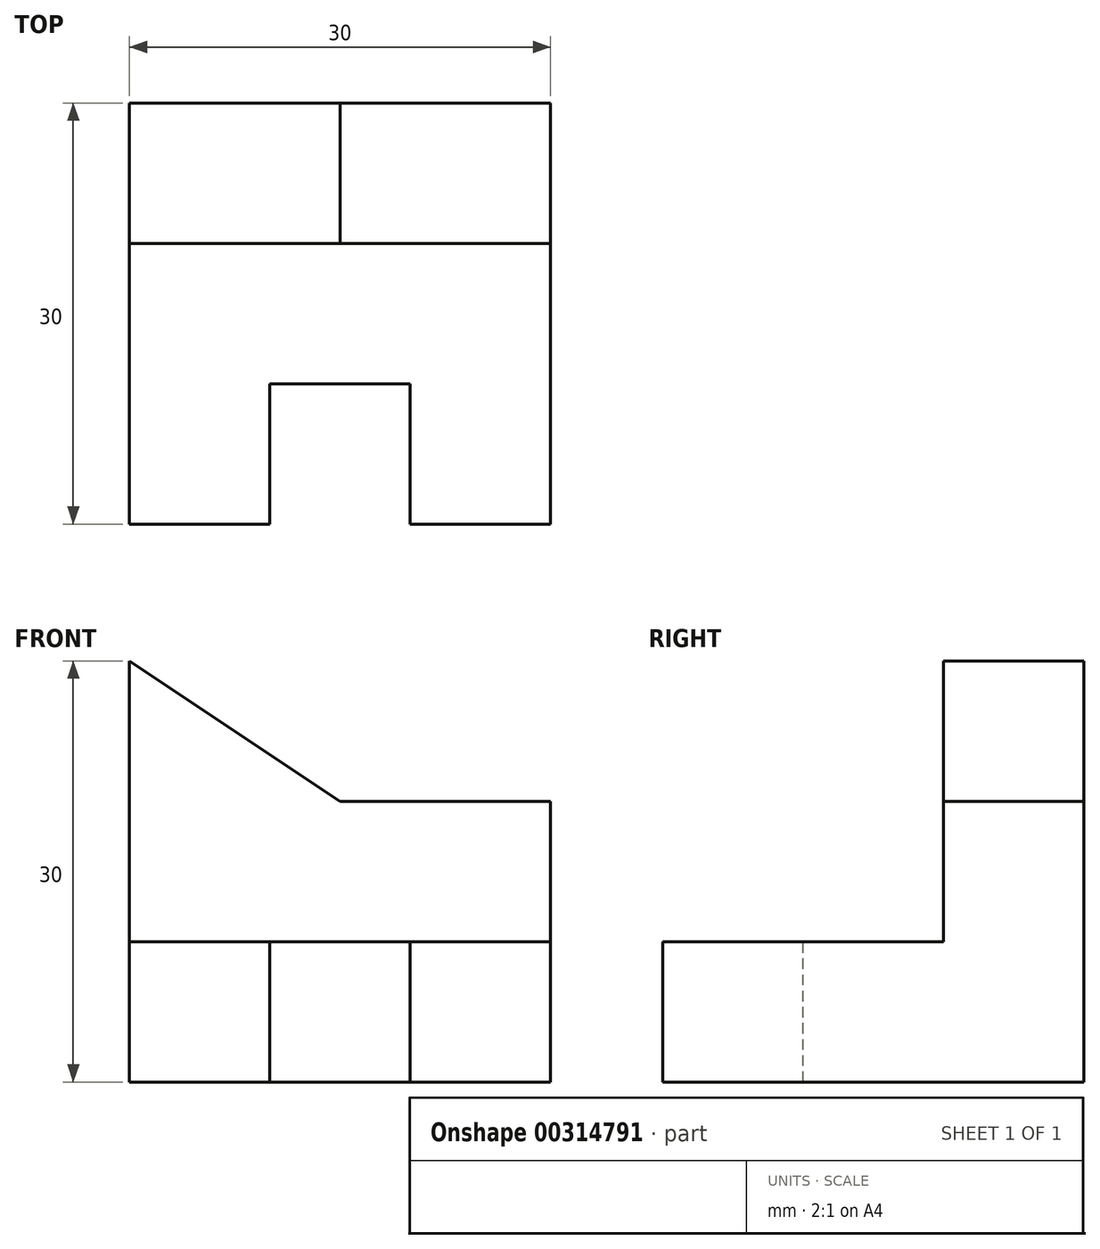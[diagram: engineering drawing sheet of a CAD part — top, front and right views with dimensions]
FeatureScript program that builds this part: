
annotation { "Feature Type Name" : "Feature", "Feature Type Description" : "" }
export const myFeature = defineFeature(function(context is Context, id is Id, definition is map)
    precondition{}
    {
        {
            var Q0;
            Q0=qCreatedBy(makeId("Right.planeOp"),FACE);
            var sketch = newSketch(context, id + "F0", { "sketchPlane" : qUnion([Q0])});
            skLineSegment(sketch, "E0.bottom", {"start": v(0, 0) * mm, "end": v(30, 0) * mm});
            skLineSegment(sketch, "E0.top", {"start": v(0, 30) * mm, "end": v(30, 30) * mm});
            skLineSegment(sketch, "E0.left", {"start": v(0, 0) * mm, "end": v(0, 30) * mm});
            skLineSegment(sketch, "E0.right", {"start": v(30, 0) * mm, "end": v(30, 30) * mm});
            skLineSegment(sketch, "E1.bottom", {"start": v(0, 30) * mm, "end": v(20, 30) * mm});
            skLineSegment(sketch, "E1.top", {"start": v(0, 10) * mm, "end": v(20, 10) * mm});
            skLineSegment(sketch, "E1.left", {"start": v(0, 30) * mm, "end": v(0, 10) * mm});
            skLineSegment(sketch, "E1.right", {"start": v(20, 30) * mm, "end": v(20, 10) * mm});
            skSolve(sketch);
        }
        {
            var Q0;
            {var subQ1=sQuery(id+"F0.wireOp",EDGE,"E0.bottom");Q0=makeQuery(id+"F0.imprint","IMPRINT",FACE,{"disambiguationData":[TD([[makeQuery(id+"F0.imprint","IMPRINT",EDGE,{"derivedFrom":subQ1}),1.0]])]});}
            extrude(context, id + "F1", {"entities" : qUnion([Q0]), "depth" : 30 * mm, "symmetric" : true});
        }
        {
            var Q0;
            Q0=makeQuery(id+"F1.opExtrude","SWEPT_FACE",FACE,{"disambiguationData":[OSD([sQuery(id+"F0.wireOp",EDGE,"E1.right")])]});
            var sketch = newSketch(context, id + "F2", { "sketchPlane" : qUnion([Q0])});
            skLineSegment(sketch, "E2", {"start": v(-15, 30) * mm, "end": v(0, 20) * mm});
            skPoint(sketch, "E2.endSnap0", {"position": v(15, 20) * mm});
            skPoint(sketch, "E2.endSnap1", {"position": v(0, 30) * mm});
            skLineSegment(sketch, "E3", {"start": v(0, 20) * mm, "end": v(15, 20) * mm});
            skSolve(sketch);
        }
        {
            var Q0;
            Q0=makeQuery(id+"F1.opExtrude","SWEPT_FACE",FACE,{"disambiguationData":[OSD([sQuery(id+"F0.wireOp",EDGE,"E1.top")])]});
            var sketch = newSketch(context, id + "F3", { "sketchPlane" : qUnion([Q0])});
            skLineSegment(sketch, "E4.bottom", {"start": v(-5, 0) * mm, "end": v(5, 0) * mm});
            skLineSegment(sketch, "E4.top", {"start": v(-5, 10) * mm, "end": v(5, 10) * mm});
            skLineSegment(sketch, "E4.left", {"start": v(-5, 0) * mm, "end": v(-5, 10) * mm});
            skLineSegment(sketch, "E4.right", {"start": v(5, 0) * mm, "end": v(5, 10) * mm});
            skSolve(sketch);
        }
        {
            var Q0;
            Q0 = qSketchRegion(id + "F2", true);
            var Q1;
            Q1=makeQuery(id+"F2.imprint","IMPRINT",FACE,{"disambiguationData":[TD([[makeQuery(id+"F2.imprint","IMPRINT",EDGE,{"derivedFrom":sQuery(id+"F2.wireOp",EDGE,"E2")}),1.0]])]});
            extrude(context, id + "F4", {"entities" : qUnion([Q0, Q1]), "operationType" : NewBodyOperationType.REMOVE, "endBound" : BoundingType.THROUGH_ALL, "oppositeDirection" : true, "depth" : 25 * mm});
        }
        {
            var Q0;
            Q0 = qSketchRegion(id + "F3", true);
            extrude(context, id + "F5", {"entities" : qUnion([Q0]), "operationType" : NewBodyOperationType.REMOVE, "endBound" : BoundingType.THROUGH_ALL, "oppositeDirection" : true, "depth" : 25 * mm});
        }
    });
